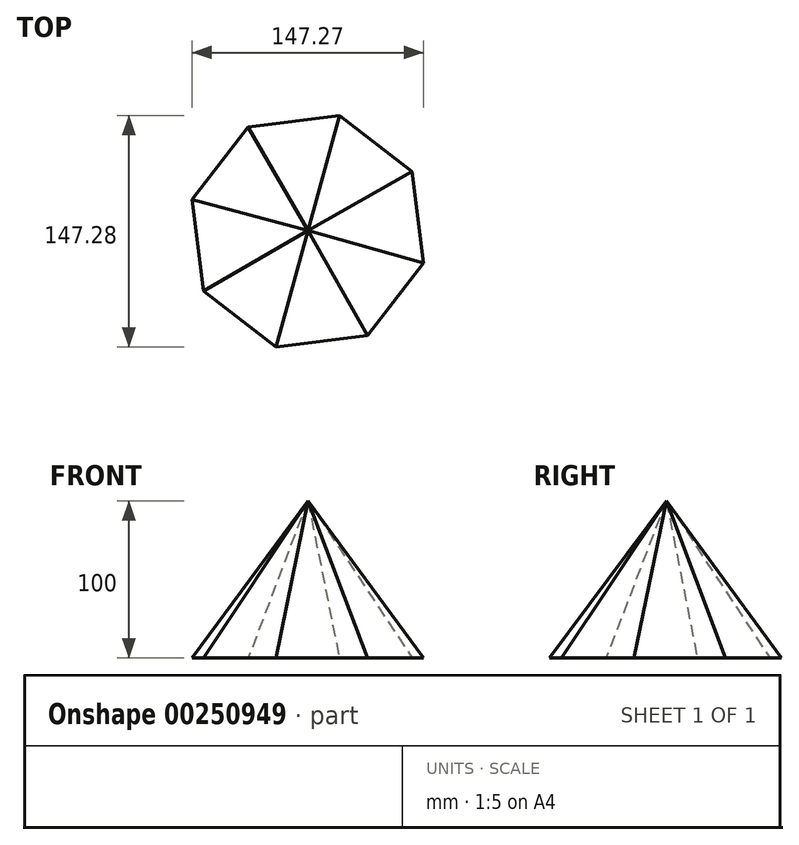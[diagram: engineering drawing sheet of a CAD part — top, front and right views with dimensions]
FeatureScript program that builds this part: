
annotation { "Feature Type Name" : "Feature", "Feature Type Description" : "" }
export const myFeature = defineFeature(function(context is Context, id is Id, definition is map)
    precondition{}
    {
        {
            var Q0;
            Q0=qCreatedBy(makeId("Top.planeOp"),FACE);
            var sketch = newSketch(context, id + "F0", { "sketchPlane" : qUnion([Q0])});
            skCircle(sketch, "E0.cCircle", {"center": v(0.57, -0.43) * mm, "radius": 76.33 * mm, "construction": true});
            skLineSegment(sketch, "E0.0", {"start": v(-37.3, 65.84) * mm, "end": v(20.66, 73.2) * mm});
            skLineSegment(sketch, "E0.1", {"start": v(20.66, 73.2) * mm, "end": v(66.84, 37.44) * mm});
            skLineSegment(sketch, "E0.2", {"start": v(66.84, 37.44) * mm, "end": v(74.21, -20.51) * mm});
            skLineSegment(sketch, "E0.3", {"start": v(74.21, -20.51) * mm, "end": v(38.44, -66.7) * mm});
            skLineSegment(sketch, "E0.4", {"start": v(38.44, -66.7) * mm, "end": v(-19.5, -74.07) * mm});
            skLineSegment(sketch, "E0.5", {"start": v(-19.5, -74.07) * mm, "end": v(-65.7, -38.3) * mm});
            skLineSegment(sketch, "E0.6", {"start": v(-65.7, -38.3) * mm, "end": v(-73.06, 19.65) * mm});
            skLineSegment(sketch, "E0.7", {"start": v(-73.06, 19.65) * mm, "end": v(-37.3, 65.84) * mm});
            skPoint(sketch, "E1", {"position": v(0.57, 0) * mm});
            skSolve(sketch);
        }
        {
            var Q0;
            Q0=qCreatedBy(makeId("Top.planeOp"),FACE);
            cPlane(context, id + "F1", {"entities" : qUnion([Q0]), "cplaneType" : CPlaneType.OFFSET, "offset" : 100 * mm, "width" : 150 * mm, "height" : 150 * mm});
        }
        {
            var Q0;
            Q0=qCreatedBy(id+"F1.planeOp",FACE);
            var sketch = newSketch(context, id + "F2", { "sketchPlane" : qUnion([Q0])});
            skPoint(sketch, "E2", {"position": v(0.57, 0) * mm});
            skSolve(sketch);
        }
        {
            var Q0;
            Q0=sQuery(id+"F2.wireOp",VERTEX,"E2");
            var Q1;
            Q1=makeQuery(id+"F0.imprint","IMPRINT",FACE,{"disambiguationData":[TD([[makeQuery(id+"F0.imprint","IMPRINT",EDGE,{"derivedFrom":sQuery(id+"F0.wireOp",EDGE,"E0.0")}),-1.0]])]});
            loft(context, id + "F3", {"sheetProfilesArray" : [{ "sheetProfileEntities" : qUnion([Q0]) }, { "sheetProfileEntities" : qUnion([Q1]) }]});
        }
    });
